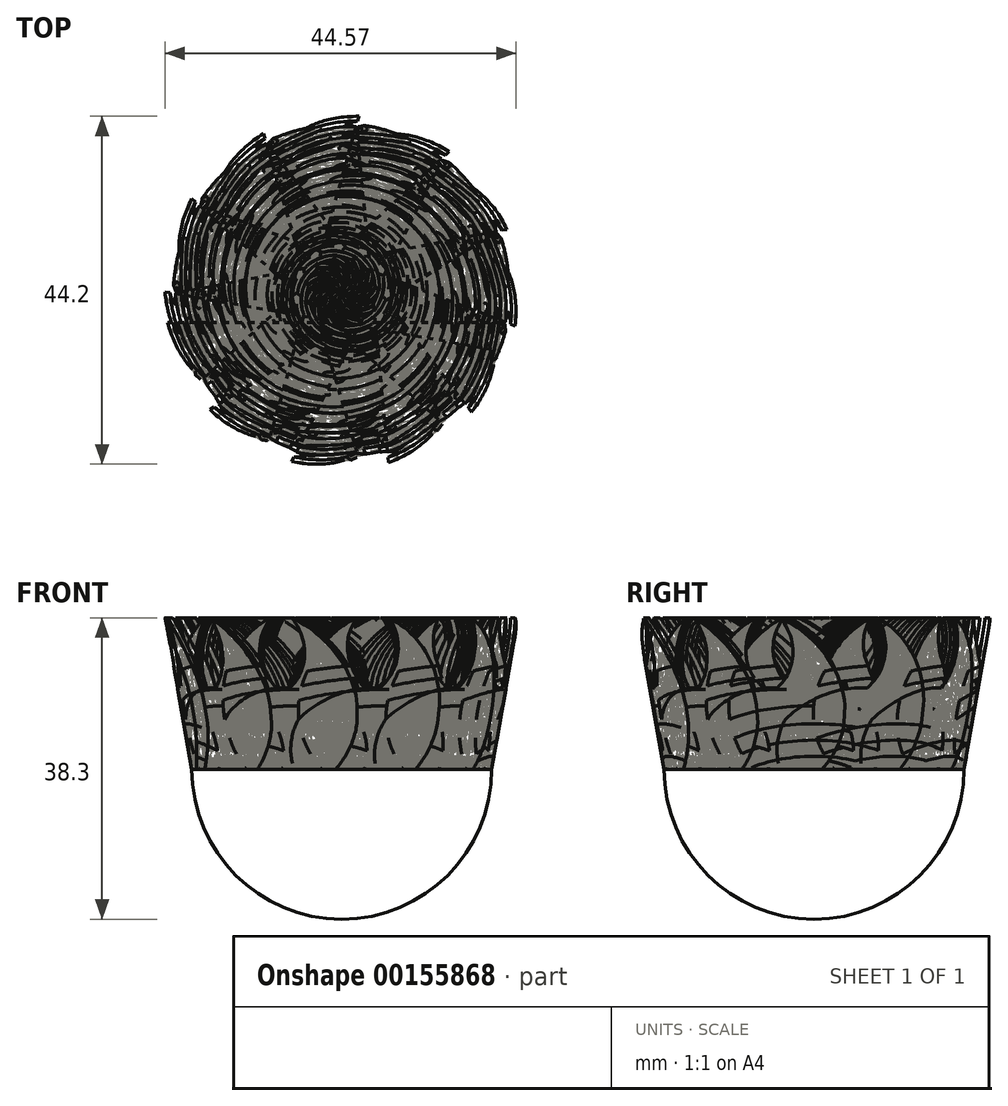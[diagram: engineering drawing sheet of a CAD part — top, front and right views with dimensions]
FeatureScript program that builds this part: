
annotation { "Feature Type Name" : "Feature", "Feature Type Description" : "" }
export const myFeature = defineFeature(function(context is Context, id is Id, definition is map)
    precondition{}
    {
        {
            var Q0;
            Q0=qCreatedBy(makeId("Top.planeOp"),FACE);
            var sketch = newSketch(context, id + "F0", { "sketchPlane" : qUnion([Q0])});
            skArc(sketch, "E0", {"start": v(0, -19.05) * mm, "mid": v(19.05, 0) * mm, "end": v(0, 19.05) * mm});
            skLineSegment(sketch, "E1", {"start": v(0, 31.17) * mm, "end": v(0, -28.33) * mm});
            skSolve(sketch);
        }
        {
            var Q0;
            {var subQ0=sQuery(id+"F0.wireOp",EDGE,"E0");Q0=makeQuery(id+"F0.imprint","IMPRINT",FACE,{"disambiguationData":[TD([[makeQuery(id+"F0.imprint","IMPRINT",EDGE,{"derivedFrom":subQ0}),1.0]])]});}
            var Q1;
            Q1=sQuery(id+"F0.wireOp",EDGE,"E1");
            revolve(context, id + "F1", {"entities" : qUnion([Q0]), "axis" : qUnion([Q1]), "revolveType" : RevolveType.ONE_DIRECTION, "oppositeDirection" : true, "angle" : 180 * degree});
        }
        {
            var Q0;
            Q0=makeQuery(id+"F1.opRevolve","CAP_FACE",FACE,{"disambiguationData":[OSD([sQuery(id+"F0.wireOp",EDGE,"E0"),sQuery(id+"F0.wireOp",EDGE,"E1")])],"isStart":true});
            var sketch = newSketch(context, id + "F2", { "sketchPlane" : qUnion([Q0])});
            skCircle(sketch, "E2.0.0", {"center": v(0, 0) * mm, "radius": 19.05 * mm});
            skSolve(sketch);
        }
        {
            var Q0;
            Q0 = qSketchRegion(id + "F2", true);
            extrude(context, id + "F3", {"entities" : qUnion([Q0]), "operationType" : NewBodyOperationType.ADD, "depth" : 25.4 * mm, "hasDraft" : true, "draftAngle" : 10 * degree});
        }
        {
            var Q0;
            Q0=makeQuery(id+"F3.opExtrude","CAP_FACE",FACE,{"disambiguationData":[OSD([sQuery(id+"F2.wireOp",EDGE,"E2.0.0")])],"isStart":false});
            var sketch = newSketch(context, id + "F4", { "sketchPlane" : qUnion([Q0])});
            skCircle(sketch, "E3", {"center": v(0, 0) * mm, "radius": 22.88 * mm});
            skCircle(sketch, "E4", {"center": v(0, 0) * mm, "radius": 22.2 * mm});
            skCircle(sketch, "E5", {"center": v(0, 0) * mm, "radius": 21.47 * mm});
            skCircle(sketch, "E6", {"center": v(0, 0) * mm, "radius": 20.79 * mm});
            skCircle(sketch, "E7", {"center": v(0, 0) * mm, "radius": 20.04 * mm});
            skCircle(sketch, "E8", {"center": v(0, 0) * mm, "radius": 19.27 * mm});
            skCircle(sketch, "E9", {"center": v(0, 0) * mm, "radius": 18.7 * mm});
            skCircle(sketch, "E10", {"center": v(0, 0) * mm, "radius": 18.15 * mm});
            skCircle(sketch, "E11", {"center": v(0, 0) * mm, "radius": 17.42 * mm});
            skCircle(sketch, "E12", {"center": v(0, 0) * mm, "radius": 16.6 * mm});
            skCircle(sketch, "E13", {"center": v(0, 0) * mm, "radius": 15.87 * mm});
            skCircle(sketch, "E14", {"center": v(0, 0) * mm, "radius": 15.15 * mm});
            skCircle(sketch, "E15", {"center": v(0, 0) * mm, "radius": 14.3 * mm});
            skCircle(sketch, "E16", {"center": v(0, 0) * mm, "radius": 13.49 * mm});
            skCircle(sketch, "E17", {"center": v(0, 0) * mm, "radius": 12.73 * mm});
            skCircle(sketch, "E18", {"center": v(0, 0) * mm, "radius": 12 * mm});
            skCircle(sketch, "E19", {"center": v(0, 0) * mm, "radius": 11.32 * mm});
            skCircle(sketch, "E20", {"center": v(0, 0) * mm, "radius": 10.6 * mm});
            skCircle(sketch, "E21", {"center": v(0, 0) * mm, "radius": 9.84 * mm});
            skCircle(sketch, "E22", {"center": v(0, 0) * mm, "radius": 9.18 * mm});
            skCircle(sketch, "E23", {"center": v(0, 0) * mm, "radius": 8.5 * mm});
            skCircle(sketch, "E24", {"center": v(0, 0) * mm, "radius": 7.92 * mm});
            skCircle(sketch, "E25", {"center": v(0, 0) * mm, "radius": 7.3 * mm});
            skCircle(sketch, "E26", {"center": v(0, 0) * mm, "radius": 6.7 * mm});
            skCircle(sketch, "E27", {"center": v(0, 0) * mm, "radius": 6.14 * mm});
            skCircle(sketch, "E28", {"center": v(0, 0) * mm, "radius": 5.45 * mm});
            skCircle(sketch, "E29", {"center": v(0, 0) * mm, "radius": 4.86 * mm});
            skCircle(sketch, "E30", {"center": v(0, 0) * mm, "radius": 4.15 * mm});
            skCircle(sketch, "E31", {"center": v(0, 0) * mm, "radius": 3.52 * mm});
            skCircle(sketch, "E32", {"center": v(0, 0) * mm, "radius": 3.03 * mm});
            skCircle(sketch, "E33", {"center": v(0, 0) * mm, "radius": 2.57 * mm});
            skCircle(sketch, "E34", {"center": v(0, 0) * mm, "radius": 2.07 * mm});
            skSolve(sketch);
        }
        {
            var Q0;
            Q0=qCreatedBy(makeId("Front.planeOp"),FACE);
            var sketch = newSketch(context, id + "F5", { "sketchPlane" : qUnion([Q0])});
            skLineSegment(sketch, "E35", {"start": v(23.53, 25.4) * mm, "end": v(19.05, 0) * mm});
            skLineSegment(sketch, "E36", {"start": v(-19.05, 0) * mm, "end": v(-23.53, 25.4) * mm});
            skLineSegment(sketch, "E37", {"start": v(0, 0) * mm, "end": v(0, 37.61) * mm});
            skLineSegment(sketch, "E38", {"start": v(0, 0) * mm, "end": v(-6.44, 36.52) * mm});
            skSolve(sketch);
        }
        {
            var Q0;
            Q0=makeQuery(id+"F4.imprint","IMPRINT",FACE,{"disambiguationData":[TD([[makeQuery(id+"F4.imprint","IMPRINT",EDGE,{"derivedFrom":sQuery(id+"F4.wireOp",EDGE,"E3")}),1.0]])]});
            var Q1;
            Q1=makeQuery(id+"F4.imprint","IMPRINT",FACE,{"disambiguationData":[TD([[makeQuery(id+"F4.imprint","IMPRINT",EDGE,{"derivedFrom":sQuery(id+"F4.wireOp",EDGE,"E5")}),1.0]])]});
            var Q2;
            Q2=makeQuery(id+"F4.imprint","IMPRINT",FACE,{"disambiguationData":[TD([[makeQuery(id+"F4.imprint","IMPRINT",EDGE,{"derivedFrom":sQuery(id+"F4.wireOp",EDGE,"E7")}),1.0]])]});
            var Q3;
            Q3=makeQuery(id+"F4.imprint","IMPRINT",FACE,{"disambiguationData":[TD([[makeQuery(id+"F4.imprint","IMPRINT",EDGE,{"derivedFrom":sQuery(id+"F4.wireOp",EDGE,"E9")}),1.0]])]});
            var Q4;
            Q4=makeQuery(id+"F4.imprint","IMPRINT",FACE,{"disambiguationData":[TD([[makeQuery(id+"F4.imprint","IMPRINT",EDGE,{"derivedFrom":sQuery(id+"F4.wireOp",EDGE,"E11")}),1.0]])]});
            var Q5;
            Q5=makeQuery(id+"F4.imprint","IMPRINT",FACE,{"disambiguationData":[TD([[makeQuery(id+"F4.imprint","IMPRINT",EDGE,{"derivedFrom":sQuery(id+"F4.wireOp",EDGE,"E13")}),1.0]])]});
            var Q6;
            Q6=makeQuery(id+"F4.imprint","IMPRINT",FACE,{"disambiguationData":[TD([[makeQuery(id+"F4.imprint","IMPRINT",EDGE,{"derivedFrom":sQuery(id+"F4.wireOp",EDGE,"E15")}),1.0]])]});
            var Q7;
            Q7=makeQuery(id+"F4.imprint","IMPRINT",FACE,{"disambiguationData":[TD([[makeQuery(id+"F4.imprint","IMPRINT",EDGE,{"derivedFrom":sQuery(id+"F4.wireOp",EDGE,"E17")}),1.0]])]});
            var Q8;
            Q8=makeQuery(id+"F4.imprint","IMPRINT",FACE,{"disambiguationData":[TD([[makeQuery(id+"F4.imprint","IMPRINT",EDGE,{"derivedFrom":sQuery(id+"F4.wireOp",EDGE,"E19")}),1.0]])]});
            var Q9;
            Q9=makeQuery(id+"F4.imprint","IMPRINT",FACE,{"disambiguationData":[TD([[makeQuery(id+"F4.imprint","IMPRINT",EDGE,{"derivedFrom":sQuery(id+"F4.wireOp",EDGE,"E21")}),1.0]])]});
            var Q10;
            Q10=makeQuery(id+"F4.imprint","IMPRINT",FACE,{"disambiguationData":[TD([[makeQuery(id+"F4.imprint","IMPRINT",EDGE,{"derivedFrom":sQuery(id+"F4.wireOp",EDGE,"E23")}),1.0]])]});
            var Q11;
            Q11=makeQuery(id+"F4.imprint","IMPRINT",FACE,{"disambiguationData":[TD([[makeQuery(id+"F4.imprint","IMPRINT",EDGE,{"derivedFrom":sQuery(id+"F4.wireOp",EDGE,"E25")}),1.0]])]});
            var Q12;
            Q12=makeQuery(id+"F4.imprint","IMPRINT",FACE,{"disambiguationData":[TD([[makeQuery(id+"F4.imprint","IMPRINT",EDGE,{"derivedFrom":sQuery(id+"F4.wireOp",EDGE,"E27")}),1.0]])]});
            var Q13;
            Q13=makeQuery(id+"F4.imprint","IMPRINT",FACE,{"disambiguationData":[TD([[makeQuery(id+"F4.imprint","IMPRINT",EDGE,{"derivedFrom":sQuery(id+"F4.wireOp",EDGE,"E29")}),1.0]])]});
            var Q14;
            Q14=makeQuery(id+"F4.imprint","IMPRINT",FACE,{"disambiguationData":[TD([[makeQuery(id+"F4.imprint","IMPRINT",EDGE,{"derivedFrom":sQuery(id+"F4.wireOp",EDGE,"E31")}),1.0]])]});
            var Q15;
            Q15=makeQuery(id+"F4.imprint","IMPRINT",FACE,{"disambiguationData":[TD([[makeQuery(id+"F4.imprint","IMPRINT",EDGE,{"derivedFrom":sQuery(id+"F4.wireOp",EDGE,"E33")}),1.0]])]});
            var Q16;
            Q16=sQuery(id+"F5.wireOp",EDGE,"E38");
            sweep(context, id + "F6", {"operationType" : NewBodyOperationType.REMOVE, "profiles" : qUnion([Q0, Q1, Q2, Q3, Q4, Q5, Q6, Q7, Q8, Q9, Q10, Q11, Q12, Q13, Q14, Q15]), "path" : qUnion([Q16])});
        }
        {
            var Q0;
            Q0=qCreatedBy(makeId("Right.planeOp"),FACE);
            cPlane(context, id + "F7", {"entities" : qUnion([Q0]), "cplaneType" : CPlaneType.OFFSET, "offset" : 25.4 * mm, "oppositeDirection" : true, "width" : 152.4 * mm, "height" : 152.4 * mm});
        }
        {
            var Q0;
            Q0=qCreatedBy(id+"F7.planeOp",FACE);
            var sketch = newSketch(context, id + "F8", { "sketchPlane" : qUnion([Q0])});
            skArc(sketch, "E39", {"start": v(7.75, 0) * mm, "mid": v(8.18, 3.22) * mm, "end": v(7.33, 6.35) * mm});
            skArc(sketch, "E40", {"start": v(-3.86, 19.25) * mm, "mid": v(-5.16, 14.6) * mm, "end": v(-2.9, 10.34) * mm});
            skArc(sketch, "E41", {"start": v(-3.86, 19.25) * mm, "mid": v(-10.58, 10.6) * mm, "end": v(-7.75, 0) * mm});
            skArc(sketch, "E42", {"start": v(7.33, 6.35) * mm, "mid": v(2.64, 9.45) * mm, "end": v(-2.9, 10.34) * mm});
            skLineSegment(sketch, "E43", {"start": v(7.75, 0) * mm, "end": v(-7.75, 0) * mm});
            skLineSegment(sketch, "E44", {"start": v(7.75, 0) * mm, "end": v(26.53, 0) * mm});
            skLineSegment(sketch, "E45", {"start": v(26.53, 0) * mm, "end": v(32.26, 30.47) * mm});
            skLineSegment(sketch, "E46", {"start": v(32.26, 30.47) * mm, "end": v(-40.75, 30.47) * mm});
            skLineSegment(sketch, "E47", {"start": v(-40.75, 30.47) * mm, "end": v(-26.9, 0) * mm});
            skLineSegment(sketch, "E48", {"start": v(-26.9, 0) * mm, "end": v(-7.75, 0) * mm});
            skSolve(sketch);
        }
        {
            var Q0;
            Q0=makeQuery(id+"F8.imprint","IMPRINT",FACE,{"disambiguationData":[TD([[makeQuery(id+"F8.imprint","IMPRINT",EDGE,{"derivedFrom":sQuery(id+"F8.wireOp",EDGE,"E39")}),-1.0]])]});
            extrude(context, id + "F9", {"entities" : qUnion([Q0]), "operationType" : NewBodyOperationType.REMOVE, "depth" : 79.95 * mm});
        }
        {
            var Q0;
            Q0=makeQuery(id+"F9.boolean.opBoolean","SPLIT",BODY,{"disambiguationData":[OD(0.0)],"derivedFrom":makeQuery(id+"F6.boolean.opBoolean","SPLIT",BODY,{"disambiguationData":[OD(1.0)],"derivedFrom":makeQuery(id+"F1.opRevolve","SWEPT_BODY",BODY,{"disambiguationData":[OSD([sQuery(id+"F0.wireOp",EDGE,"E0"),sQuery(id+"F0.wireOp",EDGE,"E1")])]})})});
            deleteBodies(context, id + "F10", {"entities" : qUnion([Q0])});
        }
        {
            var Q0;
            Q0=makeQuery(id+"F9.boolean.opBoolean","SPLIT",BODY,{"disambiguationData":[OD(1.0)],"derivedFrom":makeQuery(id+"F6.boolean.opBoolean","SPLIT",BODY,{"disambiguationData":[OD(1.0)],"derivedFrom":makeQuery(id+"F1.opRevolve","SWEPT_BODY",BODY,{"disambiguationData":[OSD([sQuery(id+"F0.wireOp",EDGE,"E0"),sQuery(id+"F0.wireOp",EDGE,"E1")])]})})});
            deleteBodies(context, id + "F11", {"entities" : qUnion([Q0])});
        }
        {
            var Q0;
            Q0=qCreatedBy(makeId("Top.planeOp"),FACE);
            var sketch = newSketch(context, id + "F12", { "sketchPlane" : qUnion([Q0])});
            skFitSpline(sketch, "E49.0.0", {"points": [v(-18.79, 7.33) * mm, v(-18.6, 7.57) * mm, v(-18.25, 7.96) * mm, v(-17.82, 8.23) * mm, v(-17.51, 8.19) * mm, v(-17.42, 7.93) * mm, v(-17.4, 7.75) * mm]});
            skArc(sketch, "E49.0.1", {"start": v(-17.4, -7.75) * mm, "mid": v(-19.05, 0) * mm, "end": v(-17.4, 7.75) * mm});
            skFitSpline(sketch, "E49.0.2", {"points": [v(-17.4, -7.75) * mm, v(-17.33, -8.08) * mm, v(-17.2, -8.68) * mm, v(-16.99, -9.7) * mm, v(-16.94, -10.4) * mm, v(-17.11, -10.76) * mm, v(-17.36, -10.85) * mm, v(-17.7, -10.78) * mm, v(-18.13, -10.55) * mm, v(-18.61, -10.17) * mm, v(-19.14, -9.64) * mm, v(-19.7, -8.98) * mm, v(-20.25, -8.2) * mm, v(-20.7, -7.44) * mm, v(-21.04, -6.77) * mm, v(-21.53, -5.72) * mm, v(-21.88, -4.73) * mm, v(-22.1, -3.86) * mm]});
            skFitSpline(sketch, "E49.0.3", {"points": [v(-22.1, -3.86) * mm, v(-22, -4.11) * mm, v(-21.8, -4.54) * mm, v(-21.4, -5.13) * mm, v(-21.05, -5.29) * mm, v(-20.84, -4.97) * mm, v(-20.73, -4.5) * mm, v(-20.68, -3.82) * mm, v(-20.67, -3.23) * mm, v(-20.67, -2.9) * mm]});
            skFitSpline(sketch, "E49.0.4", {"points": [v(-20.67, -2.9) * mm, v(-20.74, -2.42) * mm, v(-20.82, -1.7) * mm, v(-20.86, -0.73) * mm, v(-20.85, 0) * mm, v(-20.81, 0.71) * mm, v(-20.72, 1.65) * mm, v(-20.58, 2.55) * mm, v(-20.38, 3.41) * mm, v(-20.2, 4.05) * mm, v(-20.01, 4.66) * mm, v(-19.73, 5.44) * mm, v(-19.33, 6.35) * mm, v(-18.97, 7.02) * mm, v(-18.79, 7.33) * mm]});
            skLineSegment(sketch, "E50.top", {"start": v(0, -28.06) * mm, "end": v(23.47, -28.06) * mm});
            skLineSegment(sketch, "E50.right", {"start": v(23.47, 0) * mm, "end": v(23.47, -28.06) * mm});
            skLineSegment(sketch, "E51.bottom", {"start": v(23.47, -28.06) * mm, "end": v(0, -28.06) * mm});
            skLineSegment(sketch, "E51.top", {"start": v(23.47, 31.75) * mm, "end": v(0, 31.75) * mm});
            skLineSegment(sketch, "E51.left", {"start": v(23.47, -28.06) * mm, "end": v(23.47, 31.75) * mm});
            skLineSegment(sketch, "E52", {"start": v(0, 0) * mm, "end": v(-17.4, 7.75) * mm});
            skLineSegment(sketch, "E53", {"start": v(0, 0) * mm, "end": v(-17.4, -10.83) * mm});
            skLineSegment(sketch, "E54", {"start": v(-17.4, -10.83) * mm, "end": v(-17.4, -28.2) * mm});
            skLineSegment(sketch, "E55", {"start": v(-17.4, -28.2) * mm, "end": v(0, -28.2) * mm});
            skLineSegment(sketch, "E56", {"start": v(0, -28.2) * mm, "end": v(0, -28.06) * mm});
            skLineSegment(sketch, "E57", {"start": v(-17.4, 7.75) * mm, "end": v(-20.91, 24.92) * mm});
            skLineSegment(sketch, "E58", {"start": v(-20.91, 24.92) * mm, "end": v(0, 31.75) * mm});
            skSolve(sketch);
        }
        {
            var Q0;
            {var subQ0=sQuery(id+"F12.wireOp",EDGE,"E57");var subQ1=sQuery(id+"F12.wireOp",EDGE,"E49.0.0");var subQ3=makeQuery(id+"F12.imprint","INTERSECT",VERTEX,{"derivedFrom":[subQ1,subQ0]});Q0=makeQuery(id+"F12.imprint","IMPRINT",FACE,{"disambiguationData":[TD([[makeQuery(id+"F12.imprint","IMPRINT",EDGE,{"disambiguationData":[TD([[subQ3,-1.0]])],"derivedFrom":subQ1}),-1.0]])]});}
            var Q1;
            {var subQ0=sQuery(id+"F12.wireOp",EDGE,"E53");var subQ1=sQuery(id+"F12.wireOp",EDGE,"E49.0.2");var subQ3=makeQuery(id+"F12.imprint","INTERSECT",VERTEX,{"derivedFrom":[subQ1,subQ0]});Q1=makeQuery(id+"F12.imprint","IMPRINT",FACE,{"disambiguationData":[TD([[makeQuery(id+"F12.imprint","IMPRINT",EDGE,{"disambiguationData":[TD([[subQ3,-1.0]])],"derivedFrom":subQ1}),-1.0]])]});}
            var Q2;
            {var subQ9=sQuery(id+"F12.wireOp",EDGE,"E51.bottom");Q2=makeQuery(id+"F12.imprint","IMPRINT",FACE,{"disambiguationData":[TD([[makeQuery(id+"F12.imprint","IMPRINT",EDGE,{"derivedFrom":subQ9}),-1.0]])]});}
            extrude(context, id + "F13", {"entities" : qUnion([Q0, Q1, Q2]), "operationType" : NewBodyOperationType.REMOVE, "depth" : 83.18 * mm});
        }
        {
            var Q0;
            Q0=qCreatedBy(makeId("Front.planeOp"),FACE);
            var sketch = newSketch(context, id + "F14", { "sketchPlane" : qUnion([Q0])});
            skLineSegment(sketch, "E59", {"start": v(0, 0) * mm, "end": v(0, 38.9) * mm});
            skSolve(sketch);
        }
        {
            var Q0;
            Q0=makeQuery(id+"F6.boolean.opBoolean","SPLIT",BODY,{"disambiguationData":[OD(0.0)],"derivedFrom":makeQuery(id+"F1.opRevolve","SWEPT_BODY",BODY,{"disambiguationData":[OSD([sQuery(id+"F0.wireOp",EDGE,"E0"),sQuery(id+"F0.wireOp",EDGE,"E1")])]})});
            var Q1;
            Q1=makeQuery(id+"F13.boolean.opBoolean","SPLIT",BODY,{"disambiguationData":[OD(4.0)],"derivedFrom":makeQuery(id+"F9.boolean.opBoolean","SPLIT",BODY,{"disambiguationData":[OD(5.0)],"derivedFrom":makeQuery(id+"F6.boolean.opBoolean","SPLIT",BODY,{"disambiguationData":[OD(1.0)],"derivedFrom":makeQuery(id+"F1.opRevolve","SWEPT_BODY",BODY,{"disambiguationData":[OSD([sQuery(id+"F0.wireOp",EDGE,"E0"),sQuery(id+"F0.wireOp",EDGE,"E1")])]})})})});
            var Q2;
            Q2=sQuery(id+"F14.wireOp",EDGE,"E59");
            circularPattern(context, id + "F15", {"entities" : qUnion([Q0, Q1]), "axis" : qUnion([Q2]), "angle" : 350 * degree, "instanceCount" : 12, "equalSpace" : true});
        }
    });
